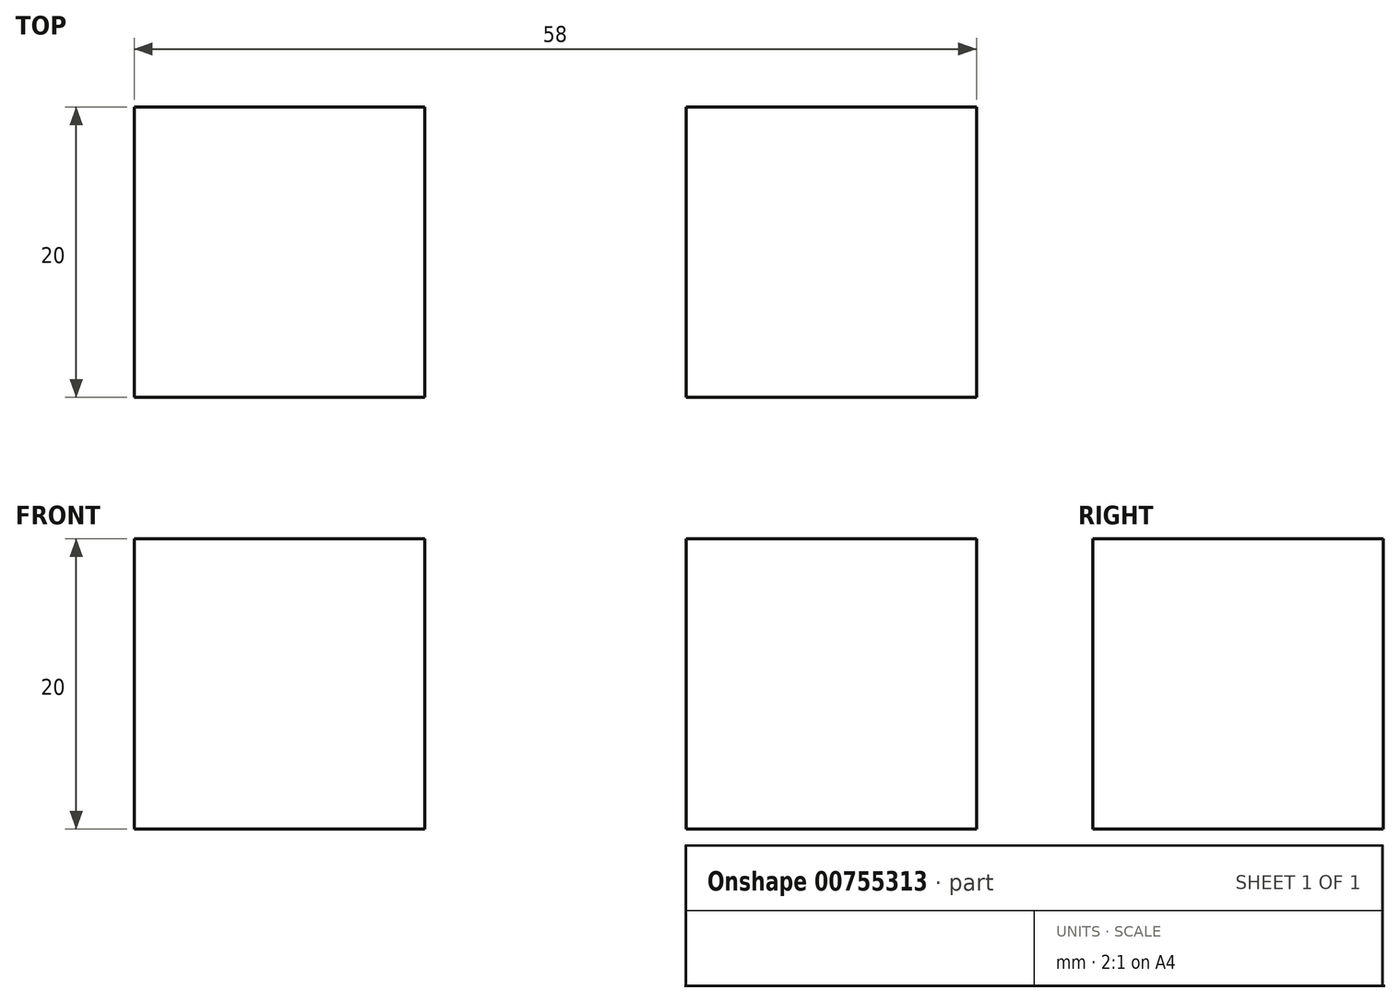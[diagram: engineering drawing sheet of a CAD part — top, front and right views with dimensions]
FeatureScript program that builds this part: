
annotation { "Feature Type Name" : "Feature", "Feature Type Description" : "" }
export const myFeature = defineFeature(function(context is Context, id is Id, definition is map)
    precondition{}
    {
        {
            var Q0;
            Q0=qCreatedBy(makeId("Top.planeOp"),FACE);
            var sketch = newSketch(context, id + "F0", { "sketchPlane" : qUnion([Q0])});
            skLineSegment(sketch, "E0.bottom", {"start": v(0, 0) * mm, "end": v(20, 0) * mm});
            skLineSegment(sketch, "E0.top", {"start": v(0, -20) * mm, "end": v(20, -20) * mm});
            skLineSegment(sketch, "E0.left", {"start": v(0, 0) * mm, "end": v(0, -20) * mm});
            skLineSegment(sketch, "E0.right", {"start": v(20, 0) * mm, "end": v(20, -20) * mm});
            skSolve(sketch);
        }
        {
            var Q0;
            Q0 = qSketchRegion(id + "F0", true);
            extrude(context, id + "F1", {"entities" : qUnion([Q0]), "depth" : 20 * mm, "offsetDistance" : 25 * mm});
        }
        {
            var Q0;
            Q0=makeQuery(id+"F1.opExtrude","SWEPT_BODY",BODY,{"disambiguationData":[OSD([sQuery(id+"F0.wireOp",EDGE,"E0.bottom"),sQuery(id+"F0.wireOp",EDGE,"E0.top"),sQuery(id+"F0.wireOp",EDGE,"E0.left"),sQuery(id+"F0.wireOp",EDGE,"E0.right")])]});
            transform(context, id + "F2", {"entities" : qUnion([Q0]), "transformType" : TransformType.TRANSLATION_3D, "dx" : 0 * mm, "dy" : 0 * mm, "dz" : 0 * mm, "makeCopy" : true});
        }
        {
            var Q0;
            Q0=makeQuery(id+"F2.opPattern","COPY",BODY,{"derivedFrom":makeQuery(id+"F1.opExtrude","SWEPT_BODY",BODY,{"disambiguationData":[OSD([sQuery(id+"F0.wireOp",EDGE,"E0.bottom"),sQuery(id+"F0.wireOp",EDGE,"E0.top"),sQuery(id+"F0.wireOp",EDGE,"E0.left"),sQuery(id+"F0.wireOp",EDGE,"E0.right")])]}),"instanceName":"1"});
            transform(context, id + "F3", {"entities" : qUnion([Q0]), "transformType" : TransformType.TRANSLATION_3D, "dx" : 38 * mm, "dy" : 0 * mm, "dz" : 0 * mm, "makeCopy" : false});
        }
    });
